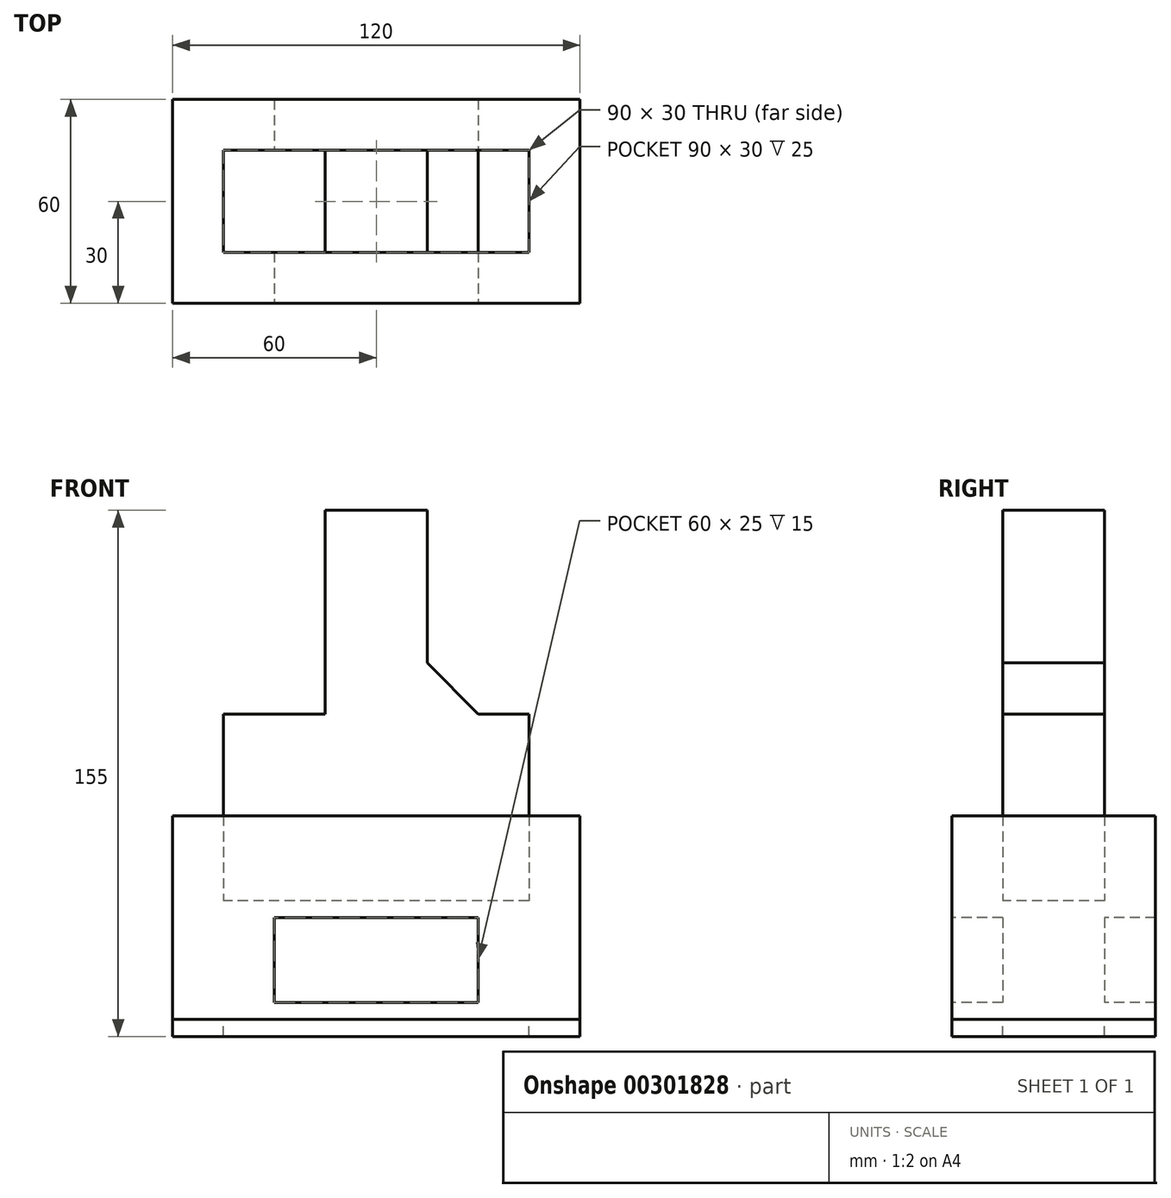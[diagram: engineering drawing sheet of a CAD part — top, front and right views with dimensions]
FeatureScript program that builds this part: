
annotation { "Feature Type Name" : "Feature", "Feature Type Description" : "" }
export const myFeature = defineFeature(function(context is Context, id is Id, definition is map)
    precondition{}
    {
        {
            var Q0;
            Q0=qCreatedBy(makeId("Top.planeOp"),FACE);
            var sketch = newSketch(context, id + "F0", { "sketchPlane" : qUnion([Q0])});
            skLineSegment(sketch, "E0.bottom", {"start": v(45, 15) * mm, "end": v(-45, 15) * mm});
            skLineSegment(sketch, "E0.top", {"start": v(45, -15) * mm, "end": v(-45, -15) * mm});
            skLineSegment(sketch, "E0.left", {"start": v(45, 15) * mm, "end": v(45, -15) * mm});
            skLineSegment(sketch, "E0.right", {"start": v(-45, 15) * mm, "end": v(-45, -15) * mm});
            skPoint(sketch, "E0.middle", {"position": v(0, 0) * mm});
            skLineSegment(sketch, "E1.bottom", {"start": v(60, -30) * mm, "end": v(-60, -30) * mm});
            skLineSegment(sketch, "E1.top", {"start": v(60, 30) * mm, "end": v(-60, 30) * mm});
            skLineSegment(sketch, "E1.left", {"start": v(60, -30) * mm, "end": v(60, 30) * mm});
            skLineSegment(sketch, "E1.right", {"start": v(-60, -30) * mm, "end": v(-60, 30) * mm});
            skLineSegment(sketch, "E2", {"start": v(-30, 30) * mm, "end": v(-30, 15) * mm});
            skLineSegment(sketch, "E3", {"start": v(-30, -15) * mm, "end": v(-30, -30) * mm});
            skLineSegment(sketch, "E4", {"start": v(30, 30) * mm, "end": v(30, 15) * mm});
            skLineSegment(sketch, "E5", {"start": v(30, -15) * mm, "end": v(30, -30) * mm});
            skSolve(sketch);
        }
        {
            var Q0;
            {var subQ0=sQuery(id+"F0.wireOp",EDGE,"E0.left");Q0=makeQuery(id+"F0.imprint","IMPRINT",FACE,{"disambiguationData":[TD([[makeQuery(id+"F0.imprint","IMPRINT",EDGE,{"derivedFrom":subQ0}),-1.0]])]});}
            extrude(context, id + "F1", {"entities" : qUnion([Q0]), "depth" : 30 * mm});
        }
        {
            var Q0;
            {var subQ3=sQuery(id+"F0.wireOp",EDGE,"E0.right");Q0=makeQuery(id+"F0.imprint","IMPRINT",FACE,{"disambiguationData":[TD([[makeQuery(id+"F0.imprint","IMPRINT",EDGE,{"derivedFrom":subQ3}),-1.0]])]});}
            var Q1;
            {var subQ0=sQuery(id+"F0.wireOp",EDGE,"E3");Q1=makeQuery(id+"F0.imprint","IMPRINT",FACE,{"disambiguationData":[TD([[makeQuery(id+"F0.imprint","IMPRINT",EDGE,{"derivedFrom":subQ0}),1.0]])]});}
            var Q2;
            {var subQ0=sQuery(id+"F0.wireOp",EDGE,"E0.left");Q2=makeQuery(id+"F0.imprint","IMPRINT",FACE,{"disambiguationData":[TD([[makeQuery(id+"F0.imprint","IMPRINT",EDGE,{"derivedFrom":subQ0}),1.0]])]});}
            var Q3;
            {var subQ0=sQuery(id+"F0.wireOp",EDGE,"E2");Q3=makeQuery(id+"F0.imprint","IMPRINT",FACE,{"disambiguationData":[TD([[makeQuery(id+"F0.imprint","IMPRINT",EDGE,{"derivedFrom":subQ0}),1.0]])]});}
            extrude(context, id + "F2", {"entities" : qUnion([Q0, Q1, Q2, Q3]), "oppositeDirection" : true, "depth" : 5 * mm});
        }
        {
            var Q0;
            {var subQ0=sQuery(id+"F0.wireOp",EDGE,"E0.left");Q0=makeQuery(id+"F0.imprint","IMPRINT",FACE,{"disambiguationData":[TD([[makeQuery(id+"F0.imprint","IMPRINT",EDGE,{"derivedFrom":subQ0}),1.0]])]});}
            var Q1;
            {var subQ3=sQuery(id+"F0.wireOp",EDGE,"E0.right");Q1=makeQuery(id+"F0.imprint","IMPRINT",FACE,{"disambiguationData":[TD([[makeQuery(id+"F0.imprint","IMPRINT",EDGE,{"derivedFrom":subQ3}),-1.0]])]});}
            extrude(context, id + "F3", {"entities" : qUnion([Q0, Q1]), "depth" : 30 * mm});
        }
        {
            var Q0;
            Q0=makeQuery(id+"F3.opExtrude","CAP_FACE",FACE,{"disambiguationData":[OSD([sQuery(id+"F0.wireOp",EDGE,"E0.bottom"),sQuery(id+"F0.wireOp",EDGE,"E0.top"),sQuery(id+"F0.wireOp",EDGE,"E0.right"),sQuery(id+"F0.wireOp",EDGE,"E1.bottom"),sQuery(id+"F0.wireOp",EDGE,"E1.top"),sQuery(id+"F0.wireOp",EDGE,"E1.right"),sQuery(id+"F0.wireOp",EDGE,"E2"),sQuery(id+"F0.wireOp",EDGE,"E3")])],"isStart":false});
            var sketch = newSketch(context, id + "F4", { "sketchPlane" : qUnion([Q0])});
            skLineSegment(sketch, "E6.bottom", {"start": v(-60, 30) * mm, "end": v(60, 30) * mm});
            skLineSegment(sketch, "E6.top", {"start": v(-60, -30) * mm, "end": v(60, -30) * mm});
            skLineSegment(sketch, "E6.left", {"start": v(-60, 30) * mm, "end": v(-60, -30) * mm});
            skLineSegment(sketch, "E6.right", {"start": v(60, 30) * mm, "end": v(60, -30) * mm});
            skPoint(sketch, "E6.middle", {"position": v(0, 0) * mm});
            skLineSegment(sketch, "E7.bottom", {"start": v(-45, 15) * mm, "end": v(45, 15) * mm});
            skLineSegment(sketch, "E7.top", {"start": v(-45, -15) * mm, "end": v(45, -15) * mm});
            skLineSegment(sketch, "E7.left", {"start": v(-45, 15) * mm, "end": v(-45, -15) * mm});
            skLineSegment(sketch, "E7.right", {"start": v(45, 15) * mm, "end": v(45, -15) * mm});
            skSolve(sketch);
        }
        {
            var Q0;
            {var subQ3=sQuery(id+"F4.wireOp",EDGE,"E6.left");Q0=makeQuery(id+"F4.imprint","IMPRINT",FACE,{"disambiguationData":[TD([[makeQuery(id+"F4.imprint","IMPRINT",EDGE,{"derivedFrom":subQ3}),-1.0]])]});}
            var Q1;
            {var subQ5=sQuery(id+"F4.wireOp",EDGE,"E6.right");Q1=makeQuery(id+"F4.imprint","IMPRINT",FACE,{"disambiguationData":[TD([[makeQuery(id+"F4.imprint","IMPRINT",EDGE,{"derivedFrom":subQ5}),-1.0]])]});}
            extrude(context, id + "F5", {"entities" : qUnion([Q0, Q1]), "depth" : 30 * mm});
        }
        {
            var Q0;
            Q0=makeQuery(id+"F5.opExtrude","CAP_FACE",FACE,{"disambiguationData":[OSD([sQuery(id+"F4.wireOp",EDGE,"E6.bottom"),sQuery(id+"F4.wireOp",EDGE,"E6.top"),sQuery(id+"F4.wireOp",EDGE,"E6.left"),sQuery(id+"F4.wireOp",EDGE,"E6.right"),sQuery(id+"F4.wireOp",EDGE,"E7.bottom"),sQuery(id+"F4.wireOp",EDGE,"E7.top"),sQuery(id+"F4.wireOp",EDGE,"E7.left"),sQuery(id+"F4.wireOp",EDGE,"E7.right")])],"isStart":false});
            var sketch = newSketch(context, id + "F6", { "sketchPlane" : qUnion([Q0])});
            skLineSegment(sketch, "E8.bottom", {"start": v(-45, 15) * mm, "end": v(45, 15) * mm});
            skLineSegment(sketch, "E8.top", {"start": v(-45, -15) * mm, "end": v(45, -15) * mm});
            skLineSegment(sketch, "E8.left", {"start": v(-45, 15) * mm, "end": v(-45, -15) * mm});
            skLineSegment(sketch, "E8.right", {"start": v(45, 15) * mm, "end": v(45, -15) * mm});
            skPoint(sketch, "E8.middle", {"position": v(0, 0) * mm});
            skSolve(sketch);
        }
        {
            var Q0;
            Q0 = qSketchRegion(id + "F6", true);
            extrude(context, id + "F7", {"entities" : qUnion([Q0]), "depth" : 30 * mm});
        }
        {
            var Q0;
            Q0=makeQuery(id+"F7.opExtrude","CAP_FACE",FACE,{"disambiguationData":[OSD([sQuery(id+"F6.wireOp",EDGE,"E8.bottom"),sQuery(id+"F6.wireOp",EDGE,"E8.top"),sQuery(id+"F6.wireOp",EDGE,"E8.left"),sQuery(id+"F6.wireOp",EDGE,"E8.right")])],"isStart":false});
            var sketch = newSketch(context, id + "F8", { "sketchPlane" : qUnion([Q0])});
            skLineSegment(sketch, "E9.bottom", {"start": v(15, 15) * mm, "end": v(-15, 15) * mm});
            skLineSegment(sketch, "E9.top", {"start": v(15, -15) * mm, "end": v(-15, -15) * mm});
            skLineSegment(sketch, "E9.left", {"start": v(15, 15) * mm, "end": v(15, -15) * mm});
            skLineSegment(sketch, "E9.right", {"start": v(-15, 15) * mm, "end": v(-15, -15) * mm});
            skPoint(sketch, "E9.middle", {"position": v(0, 0) * mm});
            skSolve(sketch);
        }
        {
            var Q0;
            Q0=makeQuery(id+"F8.imprint","IMPRINT",FACE,{"disambiguationData":[TD([[makeQuery(id+"F8.imprint","IMPRINT",EDGE,{"derivedFrom":sQuery(id+"F8.wireOp",EDGE,"E9.bottom")}),1.0]])]});
            extrude(context, id + "F9", {"entities" : qUnion([Q0]), "operationType" : NewBodyOperationType.ADD, "depth" : 60 * mm});
        }
        {
            var Q0;
            Q0=makeQuery(id+"F9.opExtrude","CAP_EDGE",EDGE,{"disambiguationData":[OSD([sQuery(id+"F8.wireOp",EDGE,"E9.left")])],"isStart":true});
            var Q1;
            Q1=makeQuery(id+"F9.opExtrude","CAP_EDGE",EDGE,{"disambiguationData":[OSD([sQuery(id+"F8.wireOp",EDGE,"E9.right")])],"isStart":true});
            chamfer(context, id + "F10", {"entities" : qUnion([Q0, Q1]), "width" : 15 * mm, "tangentPropagation" : true});
        }
        {
            var Q0;
            {var subQ3=sQuery(id+"F0.wireOp",EDGE,"E0.right");Q0=makeQuery(id+"F0.imprint","IMPRINT",FACE,{"disambiguationData":[TD([[makeQuery(id+"F0.imprint","IMPRINT",EDGE,{"derivedFrom":subQ3}),-1.0]])]});}
            var Q1;
            {var subQ0=sQuery(id+"F0.wireOp",EDGE,"E2");Q1=makeQuery(id+"F0.imprint","IMPRINT",FACE,{"disambiguationData":[TD([[makeQuery(id+"F0.imprint","IMPRINT",EDGE,{"derivedFrom":subQ0}),1.0]])]});}
            var Q2;
            {var subQ0=sQuery(id+"F0.wireOp",EDGE,"E0.left");Q2=makeQuery(id+"F0.imprint","IMPRINT",FACE,{"disambiguationData":[TD([[makeQuery(id+"F0.imprint","IMPRINT",EDGE,{"derivedFrom":subQ0}),1.0]])]});}
            var Q3;
            {var subQ0=sQuery(id+"F0.wireOp",EDGE,"E3");Q3=makeQuery(id+"F0.imprint","IMPRINT",FACE,{"disambiguationData":[TD([[makeQuery(id+"F0.imprint","IMPRINT",EDGE,{"derivedFrom":subQ0}),1.0]])]});}
            var Q4;
            {var subQ0=sQuery(id+"F0.wireOp",EDGE,"E0.left");Q4=makeQuery(id+"F0.imprint","IMPRINT",FACE,{"disambiguationData":[TD([[makeQuery(id+"F0.imprint","IMPRINT",EDGE,{"derivedFrom":subQ0}),-1.0]])]});}
            extrude(context, id + "F11", {"entities" : qUnion([Q0, Q1, Q2, Q3, Q4]), "depth" : 5 * mm});
        }
        {
            var Q0;
            Q0=makeQuery(id+"F11.opExtrude","CAP_FACE",FACE,{"disambiguationData":[OSD([sQuery(id+"F0.wireOp",EDGE,"E1.bottom"),sQuery(id+"F0.wireOp",EDGE,"E1.top"),sQuery(id+"F0.wireOp",EDGE,"E1.left"),sQuery(id+"F0.wireOp",EDGE,"E1.right")])],"isStart":false});
            var sketch = newSketch(context, id + "F12", { "sketchPlane" : qUnion([Q0])});
            skLineSegment(sketch, "E10.bottom", {"start": v(45, 15) * mm, "end": v(-45, 15) * mm});
            skLineSegment(sketch, "E10.top", {"start": v(45, -15) * mm, "end": v(-45, -15) * mm});
            skLineSegment(sketch, "E10.left", {"start": v(45, 15) * mm, "end": v(45, -15) * mm});
            skLineSegment(sketch, "E10.right", {"start": v(-45, 15) * mm, "end": v(-45, -15) * mm});
            skPoint(sketch, "E10.middle", {"position": v(0, 0) * mm});
            skSolve(sketch);
        }
        {
            var Q0;
            Q0=makeQuery(id+"F12.imprint","IMPRINT",FACE,{"disambiguationData":[TD([[makeQuery(id+"F12.imprint","IMPRINT",EDGE,{"derivedFrom":sQuery(id+"F12.wireOp",EDGE,"E10.bottom")}),1.0]])]});
            extrude(context, id + "F13", {"entities" : qUnion([Q0]), "operationType" : NewBodyOperationType.ADD, "depth" : 30 * mm});
        }
    });
